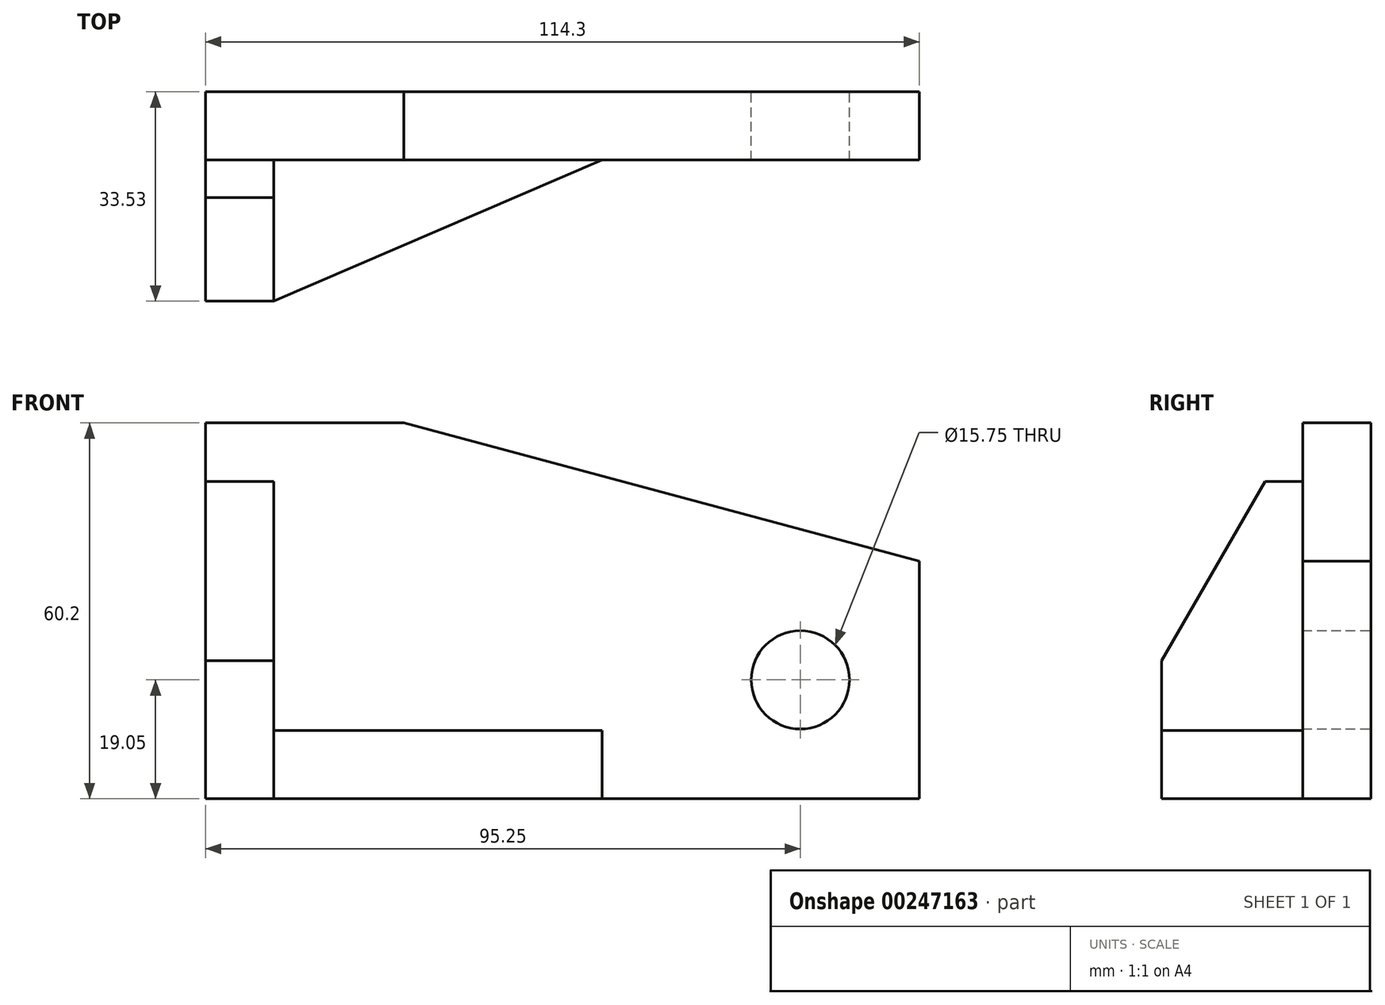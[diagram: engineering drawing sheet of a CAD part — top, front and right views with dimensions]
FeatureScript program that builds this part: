
annotation { "Feature Type Name" : "Feature", "Feature Type Description" : "" }
export const myFeature = defineFeature(function(context is Context, id is Id, definition is map)
    precondition{}
    {
        {
            var Q0;
            Q0=qCreatedBy(makeId("Front.planeOp"),FACE);
            var sketch = newSketch(context, id + "F0", { "sketchPlane" : qUnion([Q0])});
            skLineSegment(sketch, "E0", {"start": v(0, 0) * mm, "end": v(-114.3, 0) * mm});
            skLineSegment(sketch, "E1", {"start": v(-114.3, 60.2) * mm, "end": v(-82.55, 60.2) * mm});
            skLineSegment(sketch, "E2", {"start": v(0, 0) * mm, "end": v(0, 38.08) * mm});
            skLineSegment(sketch, "E3", {"start": v(-82.55, 60.2) * mm, "end": v(0, 38.08) * mm});
            skLineSegment(sketch, "E4", {"start": v(-19.05, 0) * mm, "end": v(-19.05, 19.05) * mm, "construction": true});
            skLineSegment(sketch, "E5", {"start": v(-19.05, 19.05) * mm, "end": v(0, 19.05) * mm, "construction": true});
            skCircle(sketch, "E6", {"center": v(-19.05, 19.05) * mm, "radius": 7.87 * mm});
            skLineSegment(sketch, "E7", {"start": v(-114.3, 50.8) * mm, "end": v(-103.38, 50.8) * mm});
            skLineSegment(sketch, "E8", {"start": v(-103.38, 50.8) * mm, "end": v(-103.38, 10.92) * mm});
            skLineSegment(sketch, "E9", {"start": v(-103.38, 10.92) * mm, "end": v(-50.8, 10.92) * mm});
            skLineSegment(sketch, "E10", {"start": v(-50.8, 10.92) * mm, "end": v(-50.8, 0) * mm});
            skLineSegment(sketch, "E11", {"start": v(-114.3, 0) * mm, "end": v(-114.3, 60.2) * mm});
            skSolve(sketch);
        }
        {
            var Q0;
            Q0 = qSketchRegion(id + "F0", true);
            var Q1;
            Q1=makeQuery(id+"F0.imprint","IMPRINT",FACE,{"disambiguationData":[TD([[makeQuery(id+"F0.imprint","IMPRINT",EDGE,{"derivedFrom":sQuery(id+"F0.wireOp",EDGE,"E0")}),-1.0]])]});
            extrude(context, id + "F1", {"entities" : qUnion([Q0, Q1]), "depth" : 10.92 * mm});
        }
        {
            var Q0;
            {var subQ3=sQuery(id+"F0.wireOp",EDGE,"E7");Q0=makeQuery(id+"F0.imprint","IMPRINT",FACE,{"disambiguationData":[TD([[makeQuery(id+"F0.imprint","IMPRINT",EDGE,{"derivedFrom":subQ3}),-1.0]])]});}
            extrude(context, id + "F2", {"entities" : qUnion([Q0]), "operationType" : NewBodyOperationType.ADD, "depth" : 33.53 * mm});
        }
        {
            var Q0;
            Q0=makeQuery(id+"F2.opExtrude","SWEPT_FACE",FACE,{"disambiguationData":[OSD([sQuery(id+"F0.wireOp",EDGE,"E8")])]});
            var sketch = newSketch(context, id + "F3", { "sketchPlane" : qUnion([Q0])});
            skLineSegment(sketch, "E12", {"start": v(-33.53, 22.1) * mm, "end": v(-16.96, 50.8) * mm});
            skSolve(sketch);
        }
        {
            var Q0;
            Q0 = qSketchRegion(id + "F3", true);
            var Q1;
            {var subQ0=sQuery(id+"F3.wireOp",EDGE,"E12");Q1=makeQuery(id+"F3.imprint","IMPRINT",FACE,{"disambiguationData":[TD([[makeQuery(id+"F3.imprint","IMPRINT",EDGE,{"derivedFrom":subQ0}),1.0]])]});}
            extrude(context, id + "F4", {"entities" : qUnion([Q0, Q1]), "operationType" : NewBodyOperationType.REMOVE, "depth" : 25.4 * mm});
        }
        {
            var Q0;
            {var subQ0=sQuery(id+"F3.wireOp",EDGE,"E12");Q0=makeQuery(id+"F3.imprint","IMPRINT",FACE,{"disambiguationData":[TD([[makeQuery(id+"F3.imprint","IMPRINT",EDGE,{"derivedFrom":subQ0}),1.0]])]});}
            extrude(context, id + "F5", {"entities" : qUnion([Q0]), "operationType" : NewBodyOperationType.REMOVE, "oppositeDirection" : true, "depth" : 10.92 * mm});
        }
        {
            var Q0;
            Q0=makeQuery(id+"F2.opExtrude","SWEPT_FACE",FACE,{"disambiguationData":[OSD([sQuery(id+"F0.wireOp",EDGE,"E9")])]});
            var sketch = newSketch(context, id + "F6", { "sketchPlane" : qUnion([Q0])});
            skLineSegment(sketch, "E13", {"start": v(-103.38, -33.53) * mm, "end": v(-50.8, -10.92) * mm});
            skSolve(sketch);
        }
        {
            var Q0;
            Q0=makeQuery(id+"F6.imprint","IMPRINT",FACE,{"disambiguationData":[TD([[makeQuery(id+"F6.imprint","IMPRINT",EDGE,{"derivedFrom":sQuery(id+"F6.wireOp",EDGE,"E13")}),-1.0]])]});
            extrude(context, id + "F7", {"entities" : qUnion([Q0]), "operationType" : NewBodyOperationType.REMOVE, "oppositeDirection" : true, "depth" : 10.92 * mm});
        }
    });
